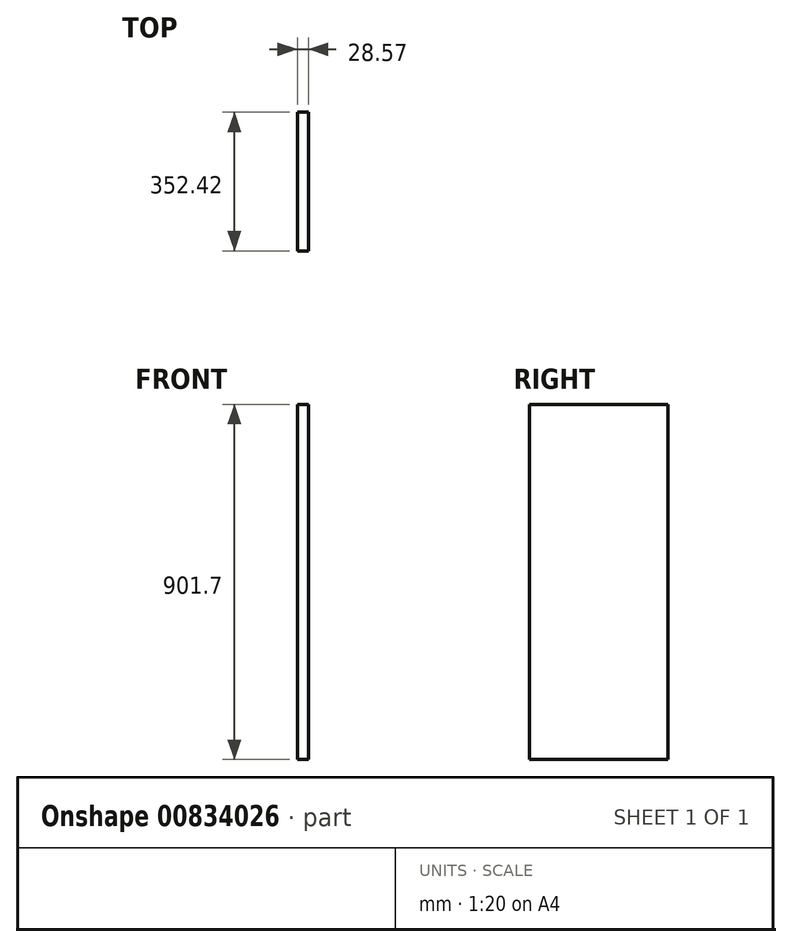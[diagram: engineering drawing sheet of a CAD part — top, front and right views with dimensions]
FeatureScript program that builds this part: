
annotation { "Feature Type Name" : "Feature", "Feature Type Description" : "" }
export const myFeature = defineFeature(function(context is Context, id is Id, definition is map)
    precondition{}
    {
        {
            var Q0;
            Q0=qCreatedBy(makeId("Right.planeOp"),FACE);
            var sketch = newSketch(context, id + "F0", { "sketchPlane" : qUnion([Q0])});
            skLineSegment(sketch, "E0.bottom", {"start": v(176.21, 450.85) * mm, "end": v(-176.21, 450.85) * mm});
            skLineSegment(sketch, "E0.top", {"start": v(176.21, -450.85) * mm, "end": v(-176.21, -450.85) * mm});
            skLineSegment(sketch, "E0.left", {"start": v(176.21, 450.85) * mm, "end": v(176.21, -450.85) * mm});
            skLineSegment(sketch, "E0.right", {"start": v(-176.21, 450.85) * mm, "end": v(-176.21, -450.85) * mm});
            skPoint(sketch, "E0.middle", {"position": v(0, 0) * mm});
            skSolve(sketch);
        }
        {
            var Q0;
            Q0=makeQuery(id+"F0.imprint","IMPRINT",FACE,{"disambiguationData":[TD([[makeQuery(id+"F0.imprint","IMPRINT",EDGE,{"derivedFrom":sQuery(id+"F0.wireOp",EDGE,"E0.bottom")}),1.0]])]});
            extrude(context, id + "F1", {"entities" : qUnion([Q0]), "depth" : 28.57 * mm, "offsetDistance" : 25.4 * mm});
        }
    });
